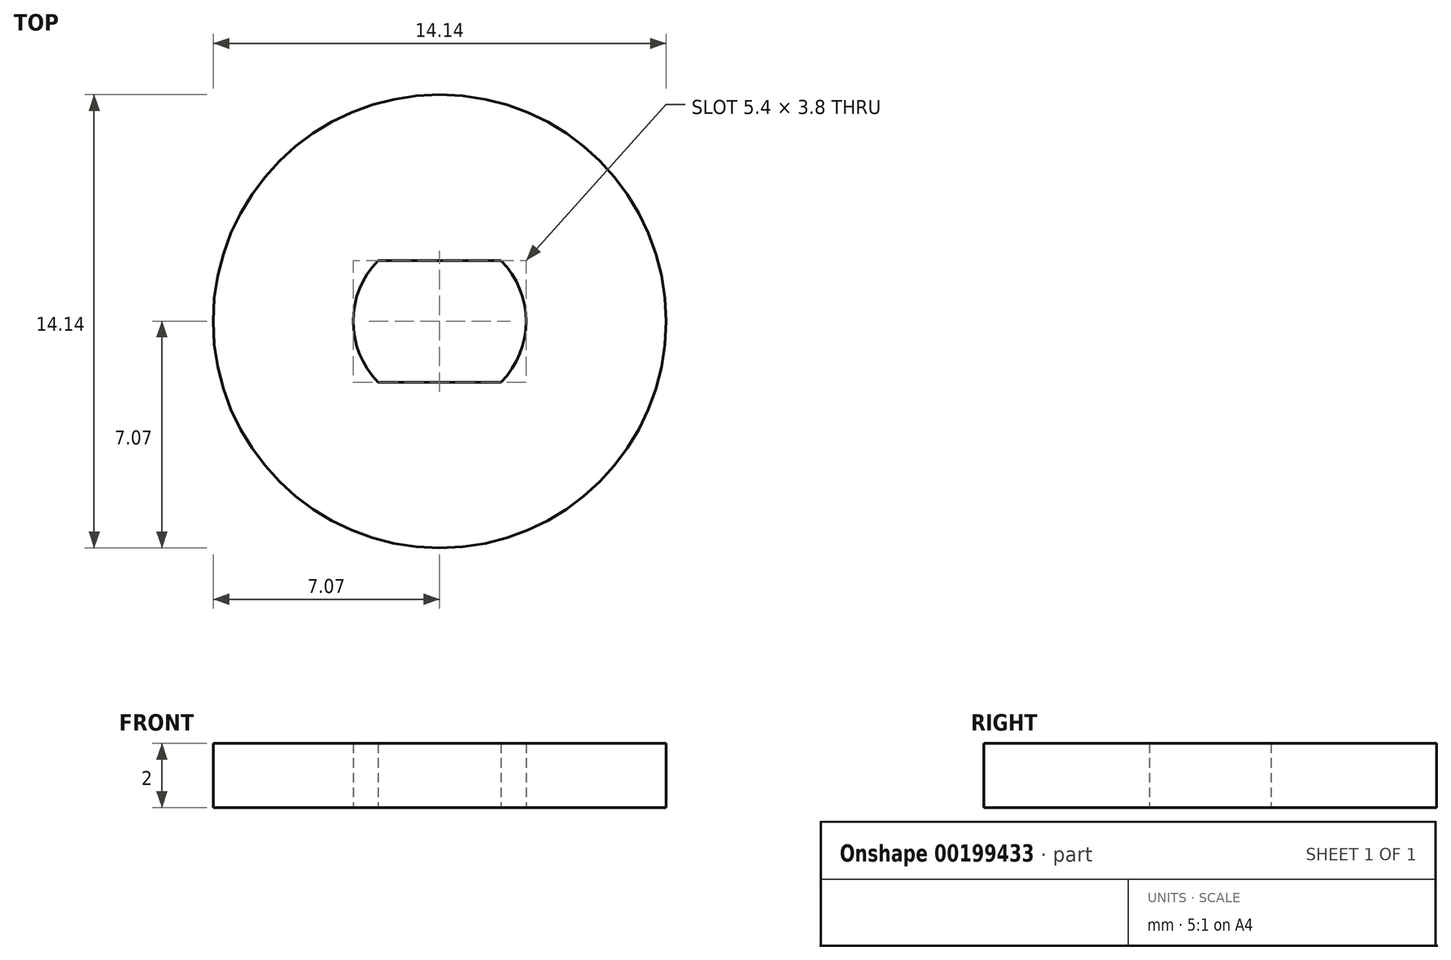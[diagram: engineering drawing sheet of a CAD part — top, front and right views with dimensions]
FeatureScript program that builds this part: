
annotation { "Feature Type Name" : "Feature", "Feature Type Description" : "" }
export const myFeature = defineFeature(function(context is Context, id is Id, definition is map)
    precondition{}
    {
        {
            var Q0;
            Q0=qCreatedBy(makeId("Top.planeOp"),FACE);
            var sketch = newSketch(context, id + "F0", { "sketchPlane" : qUnion([Q0])});
            skArc(sketch, "E0", {"start": v(-1.92, 1.9) * mm, "mid": v(-2.7, 0) * mm, "end": v(-1.92, -1.9) * mm});
            skLineSegment(sketch, "E1", {"start": v(-1.92, 1.9) * mm, "end": v(1.92, 1.9) * mm});
            skLineSegment(sketch, "E2", {"start": v(-1.92, -1.9) * mm, "end": v(1.92, -1.9) * mm});
            skArc(sketch, "E3.trimOffspring", {"start": v(1.92, -1.9) * mm, "mid": v(2.7, 0) * mm, "end": v(1.92, 1.9) * mm});
            skCircle(sketch, "E4", {"center": v(0, 0) * mm, "radius": 7.07 * mm});
            skSolve(sketch);
        }
        {
            var Q0;
            Q0 = qSketchRegion(id + "F0", true);
            extrude(context, id + "F1", {"entities" : qUnion([Q0]), "depth" : 2 * mm});
        }
    });
